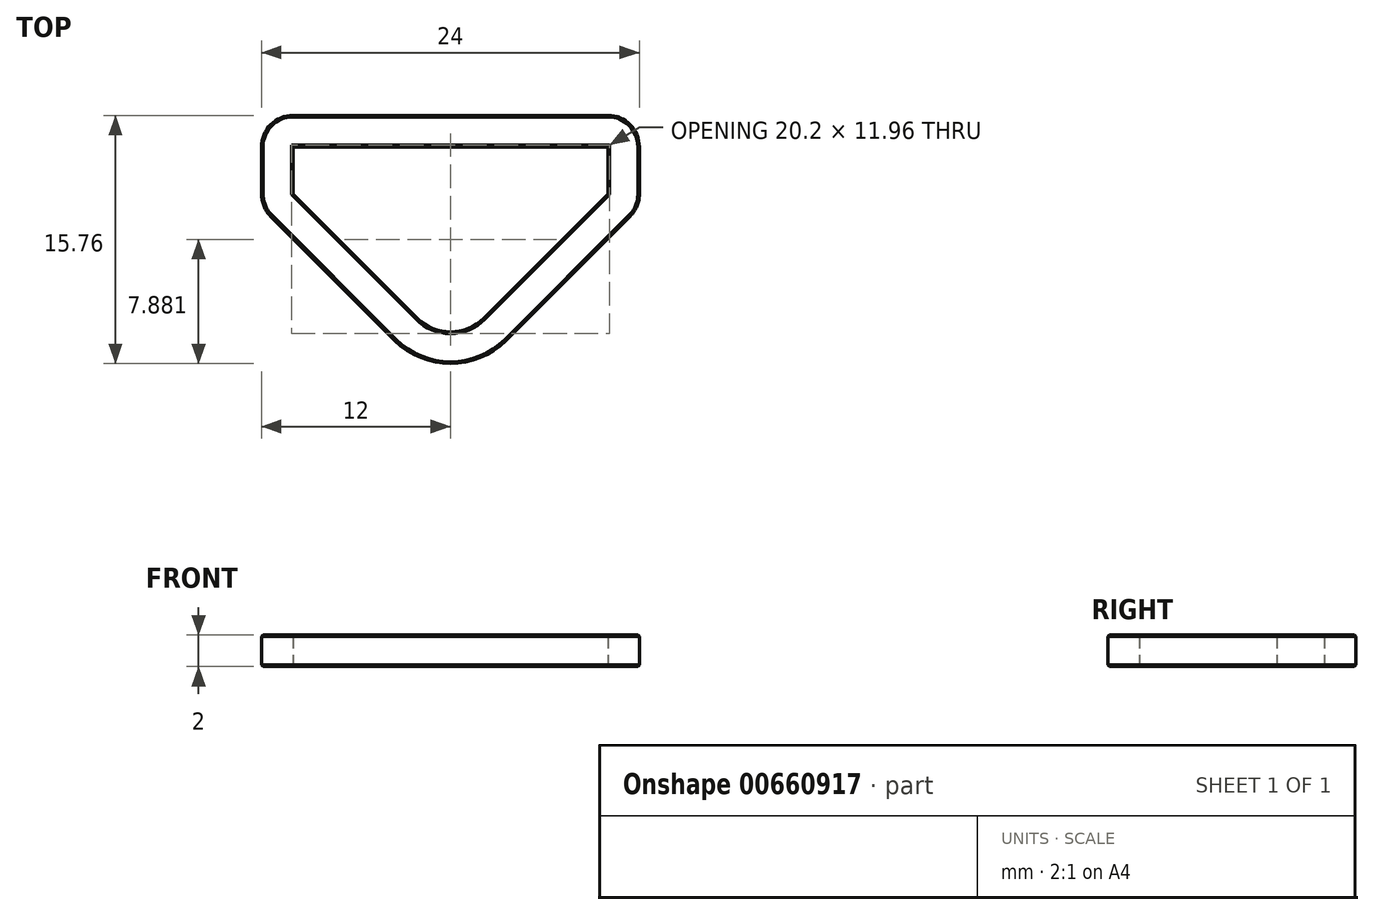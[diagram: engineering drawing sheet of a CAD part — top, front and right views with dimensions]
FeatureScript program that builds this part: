
annotation { "Feature Type Name" : "Feature", "Feature Type Description" : "" }
export const myFeature = defineFeature(function(context is Context, id is Id, definition is map)
    precondition{}
    {
        {
            var Q0;
            Q0=qCreatedBy(makeId("Top.planeOp"),FACE);
            var sketch = newSketch(context, id + "F0", { "sketchPlane" : qUnion([Q0])});
            skLineSegment(sketch, "E0.bottom", {"start": v(-10, 1.5) * mm, "end": v(10, 1.5) * mm});
            skLineSegment(sketch, "E0.top", {"start": v(-10, -1.5) * mm, "end": v(10, -1.5) * mm});
            skLineSegment(sketch, "E0.left", {"start": v(-10, 1.5) * mm, "end": v(-10, -1.5) * mm});
            skLineSegment(sketch, "E0.right", {"start": v(10, 1.5) * mm, "end": v(10, -1.5) * mm});
            skPoint(sketch, "E0.middle", {"position": v(0, 0) * mm});
            skLineSegment(sketch, "E1.bottom", {"start": v(-10, 3.5) * mm, "end": v(10, 3.5) * mm});
            skLineSegment(sketch, "E1.left", {"start": v(-10, 3.5) * mm, "end": v(-10, 1.5) * mm});
            skLineSegment(sketch, "E1.right", {"start": v(10, 3.5) * mm, "end": v(10, 1.5) * mm});
            skLineSegment(sketch, "E2.bottom", {"start": v(-12, 1.5) * mm, "end": v(-10, 1.5) * mm});
            skLineSegment(sketch, "E2.top", {"start": v(-12, -1.5) * mm, "end": v(-10, -1.5) * mm});
            skLineSegment(sketch, "E2.left", {"start": v(-12, 1.5) * mm, "end": v(-12, -1.5) * mm});
            skLineSegment(sketch, "E3.bottom", {"start": v(10, 1.5) * mm, "end": v(12, 1.5) * mm});
            skLineSegment(sketch, "E3.top", {"start": v(10, -1.5) * mm, "end": v(12, -1.5) * mm});
            skLineSegment(sketch, "E3.right", {"start": v(12, 1.5) * mm, "end": v(12, -1.5) * mm});
            skLineSegment(sketch, "E4.bottom", {"start": v(0, -1.5) * mm, "end": v(10, -1.5) * mm});
            skLineSegment(sketch, "E5.bottom", {"start": v(-10, -1.5) * mm, "end": v(0, -1.5) * mm});
            skLineSegment(sketch, "E6", {"start": v(-10, -1.5) * mm, "end": v(-2.12, -9.38) * mm});
            skLineSegment(sketch, "E7", {"start": v(2.12, -9.38) * mm, "end": v(10, -1.5) * mm});
            skLineSegment(sketch, "E8", {"start": v(-10, -1.5) * mm, "end": v(-11.41, -2.91) * mm});
            skLineSegment(sketch, "E9", {"start": v(-11.41, -2.91) * mm, "end": v(-3.54, -10.8) * mm});
            skLineSegment(sketch, "E10", {"start": v(10, -1.5) * mm, "end": v(11.41, -2.91) * mm});
            skLineSegment(sketch, "E11", {"start": v(11.41, -2.91) * mm, "end": v(3.54, -10.8) * mm});
            skLineSegment(sketch, "E12.bottom", {"start": v(-12, 3.5) * mm, "end": v(-10, 3.5) * mm});
            skLineSegment(sketch, "E12.left", {"start": v(-12, 3.5) * mm, "end": v(-12, 1.5) * mm});
            skLineSegment(sketch, "E13.bottom", {"start": v(10, 3.5) * mm, "end": v(12, 3.5) * mm});
            skLineSegment(sketch, "E13.right", {"start": v(12, 3.5) * mm, "end": v(12, 1.5) * mm});
            skLineSegment(sketch, "E14", {"start": v(12, -1.5) * mm, "end": v(12, -2.33) * mm});
            skLineSegment(sketch, "E15", {"start": v(11.41, -2.91) * mm, "end": v(12, -2.33) * mm});
            skPoint(sketch, "E16", {"position": v(12, -2.33) * mm});
            skLineSegment(sketch, "E17", {"start": v(-12, -1.5) * mm, "end": v(-12, -2.33) * mm});
            skLineSegment(sketch, "E18", {"start": v(-11.41, -2.91) * mm, "end": v(-12, -2.33) * mm});
            skPoint(sketch, "E19", {"position": v(-12, -2.33) * mm});
            skLineSegment(sketch, "E20", {"start": v(-3.54, -10.8) * mm, "end": v(-2.12, -9.38) * mm});
            skLineSegment(sketch, "E21", {"start": v(2.12, -9.38) * mm, "end": v(3.54, -10.8) * mm});
            skCircle(sketch, "E22", {"center": v(0, -7.26) * mm, "radius": 3 * mm});
            skArc(sketch, "E23", {"start": v(-3.54, -10.8) * mm, "mid": v(0, -12.26) * mm, "end": v(3.54, -10.8) * mm});
            skSolve(sketch);
        }
        {
            var Q0;
            Q0=makeQuery(id+"F0.imprint","IMPRINT",FACE,{"disambiguationData":[TD([[makeQuery(id+"F0.imprint","IMPRINT",EDGE,{"derivedFrom":sQuery(id+"F0.wireOp",EDGE,"E12.bottom")}),-1.0]])]});
            var Q1;
            Q1=makeQuery(id+"F0.imprint","IMPRINT",FACE,{"disambiguationData":[TD([[makeQuery(id+"F0.imprint","IMPRINT",EDGE,{"derivedFrom":sQuery(id+"F0.wireOp",EDGE,"E1.bottom")}),-1.0]])]});
            var Q2;
            Q2=makeQuery(id+"F0.imprint","IMPRINT",FACE,{"disambiguationData":[TD([[makeQuery(id+"F0.imprint","IMPRINT",EDGE,{"derivedFrom":sQuery(id+"F0.wireOp",EDGE,"E13.bottom")}),-1.0]])]});
            var Q3;
            Q3=makeQuery(id+"F0.imprint","IMPRINT",FACE,{"disambiguationData":[TD([[makeQuery(id+"F0.imprint","IMPRINT",EDGE,{"derivedFrom":sQuery(id+"F0.wireOp",EDGE,"E3.top")}),1.0]])]});
            var Q4;
            Q4=makeQuery(id+"F0.imprint","IMPRINT",FACE,{"disambiguationData":[TD([[makeQuery(id+"F0.imprint","IMPRINT",EDGE,{"derivedFrom":sQuery(id+"F0.wireOp",EDGE,"E3.top")}),-1.0]])]});
            var Q5;
            Q5=makeQuery(id+"F0.imprint","IMPRINT",FACE,{"disambiguationData":[TD([[makeQuery(id+"F0.imprint","IMPRINT",EDGE,{"derivedFrom":sQuery(id+"F0.wireOp",EDGE,"E7")}),-1.0]])]});
            var Q6;
            {var subQ0=sQuery(id+"F0.wireOp",EDGE,"E20");Q6=makeQuery(id+"F0.imprint","IMPRINT",FACE,{"disambiguationData":[TD([[makeQuery(id+"F0.imprint","IMPRINT",EDGE,{"derivedFrom":subQ0}),-1.0]])]});}
            var Q7;
            Q7=makeQuery(id+"F0.imprint","IMPRINT",FACE,{"disambiguationData":[TD([[makeQuery(id+"F0.imprint","IMPRINT",EDGE,{"derivedFrom":sQuery(id+"F0.wireOp",EDGE,"E6")}),-1.0]])]});
            var Q8;
            Q8=makeQuery(id+"F0.imprint","IMPRINT",FACE,{"disambiguationData":[TD([[makeQuery(id+"F0.imprint","IMPRINT",EDGE,{"derivedFrom":sQuery(id+"F0.wireOp",EDGE,"E2.top")}),-1.0]])]});
            var Q9;
            Q9=makeQuery(id+"F0.imprint","IMPRINT",FACE,{"disambiguationData":[TD([[makeQuery(id+"F0.imprint","IMPRINT",EDGE,{"derivedFrom":sQuery(id+"F0.wireOp",EDGE,"E2.top")}),1.0]])]});
            var Q10;
            Q10=makeQuery(id+"F0.imprint","IMPRINT",FACE,{"disambiguationData":[TD([[makeQuery(id+"F0.imprint","IMPRINT",EDGE,{"derivedFrom":sQuery(id+"F0.wireOp",EDGE,"E4.bottom")}),-1.0]])]});
            extrude(context, id + "F1", {"entities" : qUnion([Q0, Q1, Q2, Q3, Q4, Q5, Q6, Q7, Q8, Q9, Q10]), "depth" : 2 * mm, "offsetDistance" : 25 * mm});
        }
        {
            var Q0;
            Q0=makeQuery(id+"F1.opExtrude","SWEPT_EDGE",EDGE,{"disambiguationData":[OSD([sQuery(id+"F0.wireOp",EDGE,"E12.bottom"),sQuery(id+"F0.wireOp",EDGE,"E12.left")])]});
            var Q1;
            Q1=makeQuery(id+"F1.opExtrude","SWEPT_EDGE",EDGE,{"disambiguationData":[OSD([sQuery(id+"F0.wireOp",EDGE,"E17"),sQuery(id+"F0.wireOp",EDGE,"E18")])]});
            var Q2;
            Q2=makeQuery(id+"F1.opExtrude","SWEPT_EDGE",EDGE,{"disambiguationData":[OSD([sQuery(id+"F0.wireOp",EDGE,"E14"),sQuery(id+"F0.wireOp",EDGE,"E15")])]});
            var Q3;
            Q3=makeQuery(id+"F1.opExtrude","SWEPT_EDGE",EDGE,{"disambiguationData":[OSD([sQuery(id+"F0.wireOp",EDGE,"E13.bottom"),sQuery(id+"F0.wireOp",EDGE,"E13.right")])]});
            fillet(context, id + "F2", {"entities" : qUnion([Q0, Q1, Q2, Q3]), "radius" : 2 * mm, "tangentPropagation" : true, "allowEdgeOverflow" : false});
        }
        {
            var Q0;
            Q0=makeQuery(id+"F1.opExtrude","CAP_FACE",FACE,{"disambiguationData":[OSD([sQuery(id+"F0.wireOp",EDGE,"E1.bottom"),sQuery(id+"F0.wireOp",EDGE,"E0.bottom"),sQuery(id+"F0.wireOp",EDGE,"E2.left"),sQuery(id+"F0.wireOp",EDGE,"E0.left"),sQuery(id+"F0.wireOp",EDGE,"E0.right"),sQuery(id+"F0.wireOp",EDGE,"E3.right"),sQuery(id+"F0.wireOp",EDGE,"E4.bottom"),sQuery(id+"F0.wireOp",EDGE,"E5.bottom"),sQuery(id+"F0.wireOp",EDGE,"E9"),sQuery(id+"F0.wireOp",EDGE,"E11"),sQuery(id+"F0.wireOp",EDGE,"E12.bottom"),sQuery(id+"F0.wireOp",EDGE,"E12.left"),sQuery(id+"F0.wireOp",EDGE,"E13.bottom"),sQuery(id+"F0.wireOp",EDGE,"E13.right"),sQuery(id+"F0.wireOp",EDGE,"E14"),sQuery(id+"F0.wireOp",EDGE,"E15"),sQuery(id+"F0.wireOp",EDGE,"E17"),sQuery(id+"F0.wireOp",EDGE,"E18"),sQuery(id+"F0.wireOp",EDGE,"E22"),sQuery(id+"F0.wireOp",EDGE,"E23")])],"isStart":false});
            var Q1;
            Q1=makeQuery(id+"F1.opExtrude","CAP_FACE",FACE,{"disambiguationData":[OSD([sQuery(id+"F0.wireOp",EDGE,"E1.bottom"),sQuery(id+"F0.wireOp",EDGE,"E0.bottom"),sQuery(id+"F0.wireOp",EDGE,"E2.left"),sQuery(id+"F0.wireOp",EDGE,"E0.left"),sQuery(id+"F0.wireOp",EDGE,"E0.right"),sQuery(id+"F0.wireOp",EDGE,"E3.right"),sQuery(id+"F0.wireOp",EDGE,"E4.bottom"),sQuery(id+"F0.wireOp",EDGE,"E5.bottom"),sQuery(id+"F0.wireOp",EDGE,"E9"),sQuery(id+"F0.wireOp",EDGE,"E11"),sQuery(id+"F0.wireOp",EDGE,"E12.bottom"),sQuery(id+"F0.wireOp",EDGE,"E12.left"),sQuery(id+"F0.wireOp",EDGE,"E13.bottom"),sQuery(id+"F0.wireOp",EDGE,"E13.right"),sQuery(id+"F0.wireOp",EDGE,"E14"),sQuery(id+"F0.wireOp",EDGE,"E15"),sQuery(id+"F0.wireOp",EDGE,"E17"),sQuery(id+"F0.wireOp",EDGE,"E18"),sQuery(id+"F0.wireOp",EDGE,"E22"),sQuery(id+"F0.wireOp",EDGE,"E23")])],"isStart":true});
            chamfer(context, id + "F3", {"entities" : qUnion([Q0, Q1]), "width" : 0.1 * mm, "tangentPropagation" : true});
        }
    });
